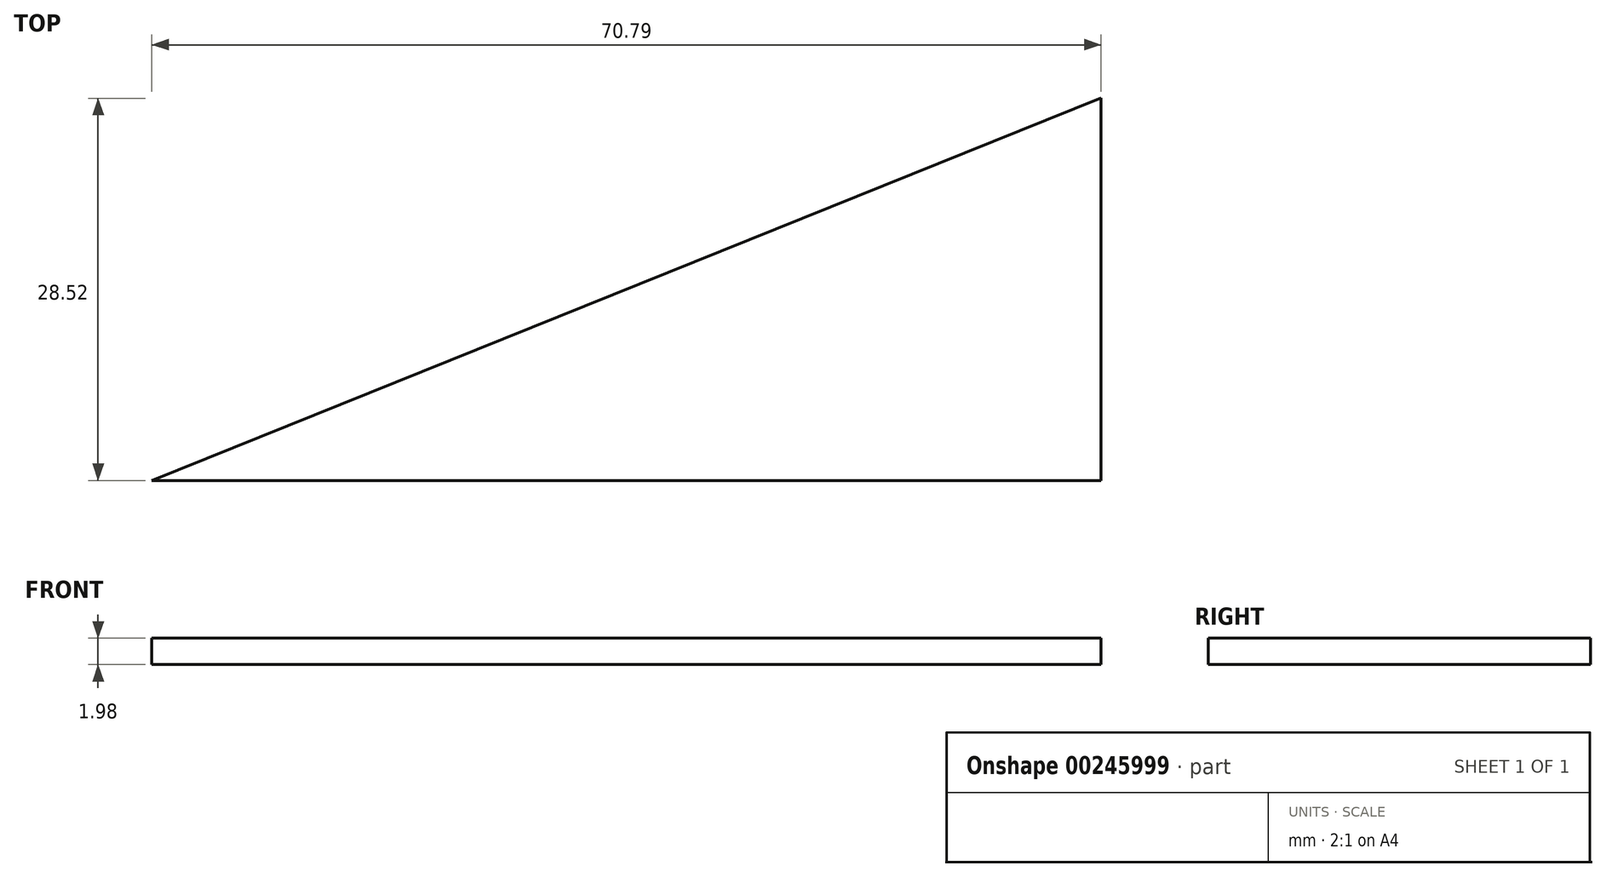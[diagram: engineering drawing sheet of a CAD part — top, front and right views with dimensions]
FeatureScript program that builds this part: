
annotation { "Feature Type Name" : "Feature", "Feature Type Description" : "" }
export const myFeature = defineFeature(function(context is Context, id is Id, definition is map)
    precondition{}
    {
        {
            var Q0;
            Q0=qCreatedBy(makeId("Top.planeOp"),FACE);
            var sketch = newSketch(context, id + "F0", { "sketchPlane" : qUnion([Q0])});
            skLineSegment(sketch, "E0", {"start": v(0, 0) * mm, "end": v(70.8, 0) * mm});
            skLineSegment(sketch, "E1", {"start": v(70.8, 0) * mm, "end": v(70.8, 28.52) * mm});
            skLineSegment(sketch, "E2", {"start": v(70.8, 28.52) * mm, "end": v(0, 0) * mm});
            skSolve(sketch);
        }
        {
            var Q0;
            Q0 = qSketchRegion(id + "F0", true);
            extrude(context, id + "F1", {"entities" : qUnion([Q0]), "depth" : 1.98 * mm});
        }
    });
